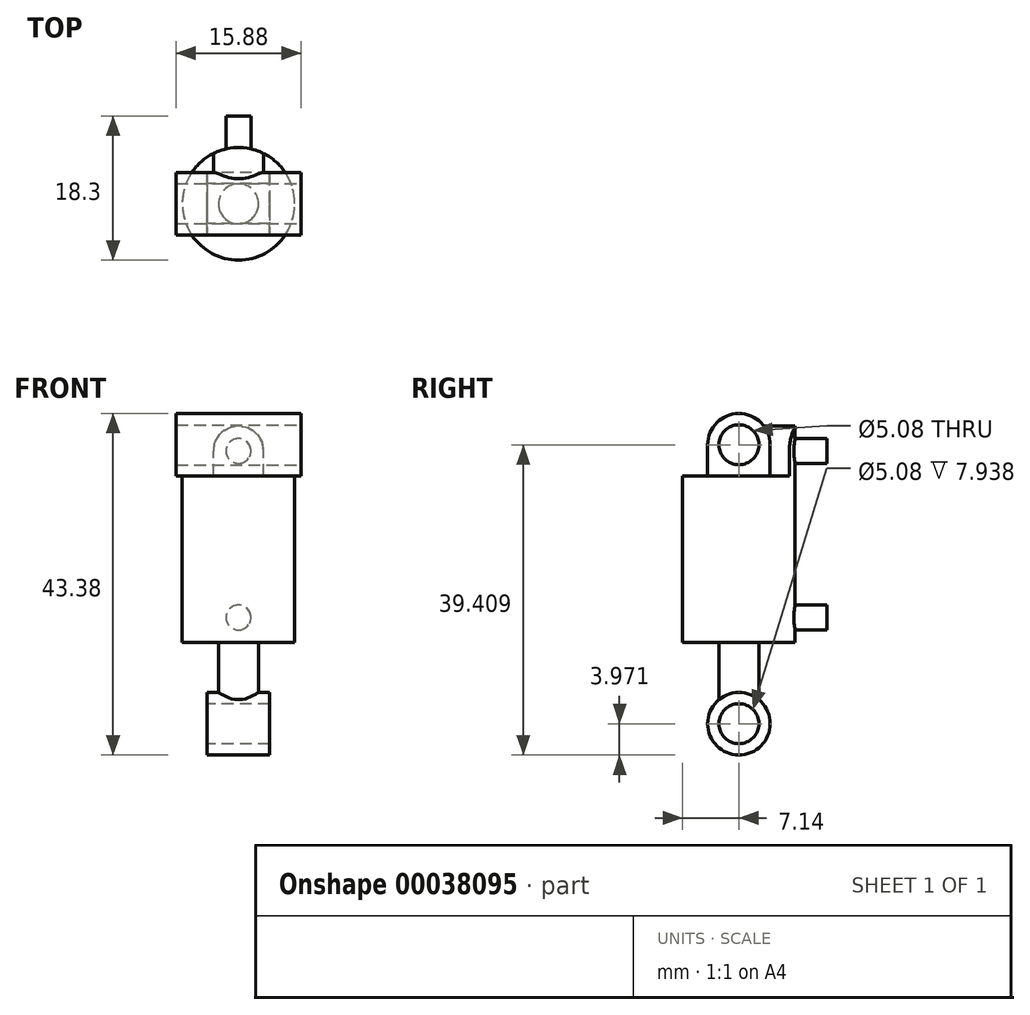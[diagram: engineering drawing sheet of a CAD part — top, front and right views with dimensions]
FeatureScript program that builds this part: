
annotation { "Feature Type Name" : "Feature", "Feature Type Description" : "" }
export const myFeature = defineFeature(function(context is Context, id is Id, definition is map)
    precondition{}
    {
        {
            var Q0;
            Q0=qCreatedBy(makeId("Top.planeOp"),FACE);
            var sketch = newSketch(context, id + "F0", { "sketchPlane" : qUnion([Q0])});
            skCircle(sketch, "E0", {"center": v(0, 0) * mm, "radius": 7.14 * mm});
            skSolve(sketch);
        }
        {
            var Q0;
            Q0=qSketchRegion(id+"F0",true);
            extrude(context, id + "F1", {"entities" : qUnion([Q0]), "depth" : 21.15 * mm});
        }
        {
            var Q0;
            Q0=makeQuery(id+"F1.opExtrude","CAP_FACE",FACE,{"disambiguationData":[OSD([sQuery(id+"F0.wireOp",EDGE,"E0")])],"isStart":false});
            var sketch = newSketch(context, id + "F2", { "sketchPlane" : qUnion([Q0])});
            skLineSegment(sketch, "E1.rect.bottom", {"start": v(7.94, 3.97) * mm, "end": v(-7.94, 3.97) * mm});
            skLineSegment(sketch, "E1.rect.top", {"start": v(7.94, -3.97) * mm, "end": v(-7.94, -3.97) * mm});
            skLineSegment(sketch, "E1.rect.left", {"start": v(7.94, 3.97) * mm, "end": v(7.94, -3.97) * mm});
            skLineSegment(sketch, "E1.rect.right", {"start": v(-7.94, 3.97) * mm, "end": v(-7.94, -3.97) * mm});
            skPoint(sketch, "E1.rect.middle", {"position": v(0, 0) * mm});
            skSolve(sketch);
        }
        {
            var Q0;
            Q0=qSketchRegion(id+"F2",true);
            extrude(context, id + "F3", {"entities" : qUnion([Q0]), "operationType" : NewBodyOperationType.ADD, "depth" : 7.94 * mm});
        }
        {
            var Q0;
            Q0=makeQuery(id+"F3.opExtrude","CAP_EDGE",EDGE,{"disambiguationData":[OSD([sQuery(id+"F2.wireOp",EDGE,"E1.rect.bottom")])],"isStart":false});
            var Q1;
            Q1=makeQuery(id+"F3.opExtrude","CAP_EDGE",EDGE,{"disambiguationData":[OSD([sQuery(id+"F2.wireOp",EDGE,"E1.rect.top")])],"isStart":false});
            fillet(context, id + "F4", {"entities" : qUnion([Q0, Q1]), "radius" : 3.97 * mm, "tangentPropagation" : true, "allowEdgeOverflow" : false});
        }
        {
            var Q0;
            Q0=makeQuery(id+"F3.opExtrude","SWEPT_FACE",FACE,{"disambiguationData":[OSD([sQuery(id+"F2.wireOp",EDGE,"E1.rect.left")])]});
            var sketch = newSketch(context, id + "F5", { "sketchPlane" : qUnion([Q0])});
            skCircle(sketch, "E2", {"center": v(0, 25.12) * mm, "radius": 2.54 * mm});
            skSolve(sketch);
        }
        {
            var Q0;
            Q0=qSketchRegion(id+"F5",true);
            var Q1;
            Q1=makeQuery(id+"F3.opExtrude","SWEPT_FACE",FACE,{"disambiguationData":[OSD([sQuery(id+"F2.wireOp",EDGE,"E1.rect.right")])]});
            extrude(context, id + "F6", {"entities" : qUnion([Q0]), "operationType" : NewBodyOperationType.REMOVE, "endBound" : BoundingType.UP_TO_SURFACE, "oppositeDirection" : true, "endBoundEntityFace" : qUnion([Q1]), "depth" : 25.4 * mm});
        }
        {
            var Q0;
            Q0=makeQuery(id+"F3.opExtrude","SWEPT_FACE",FACE,{"disambiguationData":[OSD([sQuery(id+"F2.wireOp",EDGE,"E1.rect.bottom")])]});
            var sketch = newSketch(context, id + "F7", { "sketchPlane" : qUnion([Q0])});
            skLineSegment(sketch, "E3.bottom", {"start": v(-3.18, 21.15) * mm, "end": v(3.18, 21.15) * mm});
            skLineSegment(sketch, "E3.top", {"start": v(-3.18, 24.32) * mm, "end": v(3.17, 24.32) * mm});
            skLineSegment(sketch, "E3.left", {"start": v(-3.18, 21.15) * mm, "end": v(-3.18, 24.32) * mm});
            skLineSegment(sketch, "E3.right", {"start": v(3.18, 21.15) * mm, "end": v(3.18, 24.32) * mm});
            skPoint(sketch, "E4", {"position": v(0, 21.15) * mm});
            skArc(sketch, "E5", {"start": v(3.17, 24.32) * mm, "mid": v(0, 27.5) * mm, "end": v(-3.18, 24.32) * mm});
            skSolve(sketch);
        }
        {
            var Q0;
            Q0=qSketchRegion(id+"F7",true);
            var Q1;
            Q1=makeQuery(id+"F1.opExtrude","SWEPT_FACE",FACE,{"disambiguationData":[OSD([sQuery(id+"F0.wireOp",EDGE,"E0")])]});
            var Q2;
            Q2=makeQuery(id+"F4.opFillet","BLEND_FACE",FACE,{"disambiguationData":[OSD([sQuery(id+"F2.wireOp",EDGE,"E1.rect.bottom")])]});
            extrude(context, id + "F8", {"entities" : qUnion([Q0]), "operationType" : NewBodyOperationType.ADD, "endBound" : BoundingType.UP_TO_SURFACE, "endBoundEntityFace" : qUnion([Q1]), "depth" : 25.4 * mm, "hasSecondDirection" : true, "secondDirectionBound" : SecondDirectionBoundingType.UP_TO_SURFACE, "secondDirectionOppositeDirection" : true, "secondDirectionBoundEntityFace" : qUnion([Q2]), "secondDirectionDepth" : 25.4 * mm});
        }
        {
            var Q0;
            Q0=qCreatedBy(makeId("Front.planeOp"),FACE);
            cPlane(context, id + "F9", {"entities" : qUnion([Q0]), "cplaneType" : CPlaneType.OFFSET, "offset" : 6.4 * mm, "oppositeDirection" : true, "width" : 152.4 * mm, "height" : 152.4 * mm});
        }
        {
            var Q0;
            Q0=qCreatedBy(id+"F9.planeOp",FACE);
            var sketch = newSketch(context, id + "F10", { "sketchPlane" : qUnion([Q0])});
            skCircle(sketch, "E6", {"center": v(0, 24.32) * mm, "radius": 1.59 * mm});
            skLineSegment(sketch, "E7", {"start": v(0, 24.32) * mm, "end": v(0, 3.18) * mm, "construction": true});
            skLineSegment(sketch, "E8", {"start": v(0, 3.18) * mm, "end": v(0, 0) * mm, "construction": true});
            skCircle(sketch, "E9", {"center": v(0, 3.18) * mm, "radius": 1.59 * mm});
            skSolve(sketch);
        }
        {
            var Q0;
            Q0=qSketchRegion(id+"F10",true);
            extrude(context, id + "F11", {"entities" : qUnion([Q0]), "operationType" : NewBodyOperationType.ADD, "oppositeDirection" : true, "depth" : 4.76 * mm});
        }
        {
            var Q0;
            Q0=makeQuery(id+"F1.opExtrude","CAP_FACE",FACE,{"disambiguationData":[OSD([sQuery(id+"F0.wireOp",EDGE,"E0")])],"isStart":true});
            var sketch = newSketch(context, id + "F12", { "sketchPlane" : qUnion([Q0])});
            skCircle(sketch, "E10", {"center": v(0, 0) * mm, "radius": 2.54 * mm});
            skSolve(sketch);
        }
        {
            var Q0;
            Q0=qSketchRegion(id+"F12",true);
            extrude(context, id + "F13", {"entities" : qUnion([Q0]), "operationType" : NewBodyOperationType.ADD, "depth" : 6.35 * mm});
        }
        {
            var Q0;
            Q0=makeQuery(id+"F13.opExtrude","CAP_FACE",FACE,{"disambiguationData":[OSD([sQuery(id+"F12.wireOp",EDGE,"E10")])],"isStart":false});
            var sketch = newSketch(context, id + "F14", { "sketchPlane" : qUnion([Q0])});
            skLineSegment(sketch, "E11.rect.bottom", {"start": v(3.97, 3.97) * mm, "end": v(-3.97, 3.97) * mm});
            skLineSegment(sketch, "E11.rect.top", {"start": v(3.97, -3.97) * mm, "end": v(-3.97, -3.97) * mm});
            skLineSegment(sketch, "E11.rect.left", {"start": v(3.97, 3.97) * mm, "end": v(3.97, -3.97) * mm});
            skLineSegment(sketch, "E11.rect.right", {"start": v(-3.97, 3.97) * mm, "end": v(-3.97, -3.97) * mm});
            skPoint(sketch, "E11.rect.middle", {"position": v(0, 0) * mm});
            skSolve(sketch);
        }
        {
            var Q0;
            Q0=qSketchRegion(id+"F14",true);
            extrude(context, id + "F15", {"entities" : qUnion([Q0]), "operationType" : NewBodyOperationType.ADD, "depth" : 7.94 * mm});
        }
        {
            var Q0;
            Q0=makeQuery(id+"F15.opExtrude","CAP_EDGE",EDGE,{"disambiguationData":[OSD([sQuery(id+"F14.wireOp",EDGE,"E11.rect.top")])],"isStart":true});
            var Q1;
            Q1=makeQuery(id+"F15.opExtrude","CAP_EDGE",EDGE,{"disambiguationData":[OSD([sQuery(id+"F14.wireOp",EDGE,"E11.rect.top")])],"isStart":false});
            var Q2;
            Q2=makeQuery(id+"F15.opExtrude","CAP_EDGE",EDGE,{"disambiguationData":[OSD([sQuery(id+"F14.wireOp",EDGE,"E11.rect.bottom")])],"isStart":false});
            var Q3;
            Q3=makeQuery(id+"F15.opExtrude","CAP_EDGE",EDGE,{"disambiguationData":[OSD([sQuery(id+"F14.wireOp",EDGE,"E11.rect.bottom")])],"isStart":true});
            fillet(context, id + "F16", {"entities" : qUnion([Q0, Q1, Q2, Q3]), "radius" : 3.97 * mm, "tangentPropagation" : true, "allowEdgeOverflow" : false});
        }
        {
            var Q0;
            Q0=makeQuery(id+"F15.opExtrude","SWEPT_FACE",FACE,{"disambiguationData":[OSD([sQuery(id+"F14.wireOp",EDGE,"E11.rect.right")])]});
            var sketch = newSketch(context, id + "F17", { "sketchPlane" : qUnion([Q0])});
            skCircle(sketch, "E12", {"center": v(0, -10.32) * mm, "radius": 2.54 * mm});
            skSolve(sketch);
        }
        {
            var Q0;
            Q0=qSketchRegion(id+"F17",true);
            var Q1;
            Q1=makeQuery(id+"F15.opExtrude","SWEPT_FACE",FACE,{"disambiguationData":[OSD([sQuery(id+"F14.wireOp",EDGE,"E11.rect.left")])]});
            extrude(context, id + "F18", {"entities" : qUnion([Q0]), "operationType" : NewBodyOperationType.REMOVE, "endBound" : BoundingType.UP_TO_SURFACE, "oppositeDirection" : true, "endBoundEntityFace" : qUnion([Q1]), "depth" : 25.4 * mm});
        }
    });
